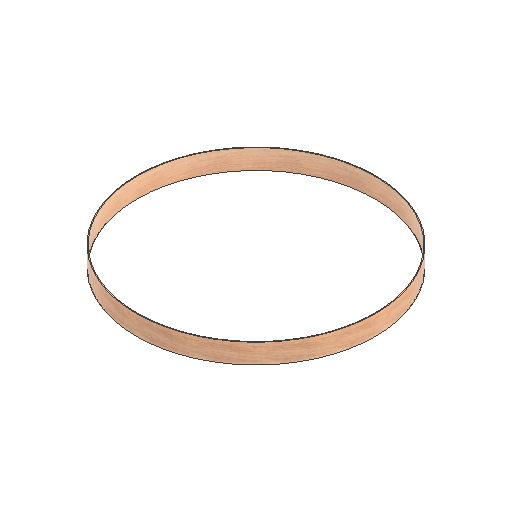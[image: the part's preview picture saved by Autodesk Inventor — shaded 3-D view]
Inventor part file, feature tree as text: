
AUTODESK INVENTOR PART (.ipt)
format: ipt  version: 2021 (Build 250183000, 183)  size: 122,368 bytes
history: native  units: mm
features: extrude x1, sketch x1
ambient origin geometry x8: Origin, YZ Plane, XZ Plane, XY Plane, X Axis, Y Axis, Z Axis, Center Point
bodies: Solid1 (feature_tree)
feature tree (2):
  extrude  "Extrusion1"  Depth=100.0mm
  sketch  "Sketch1"  dims[d0=1200.0mm d1=1208.0mm d2=100.0mm d3=0.0mm]
